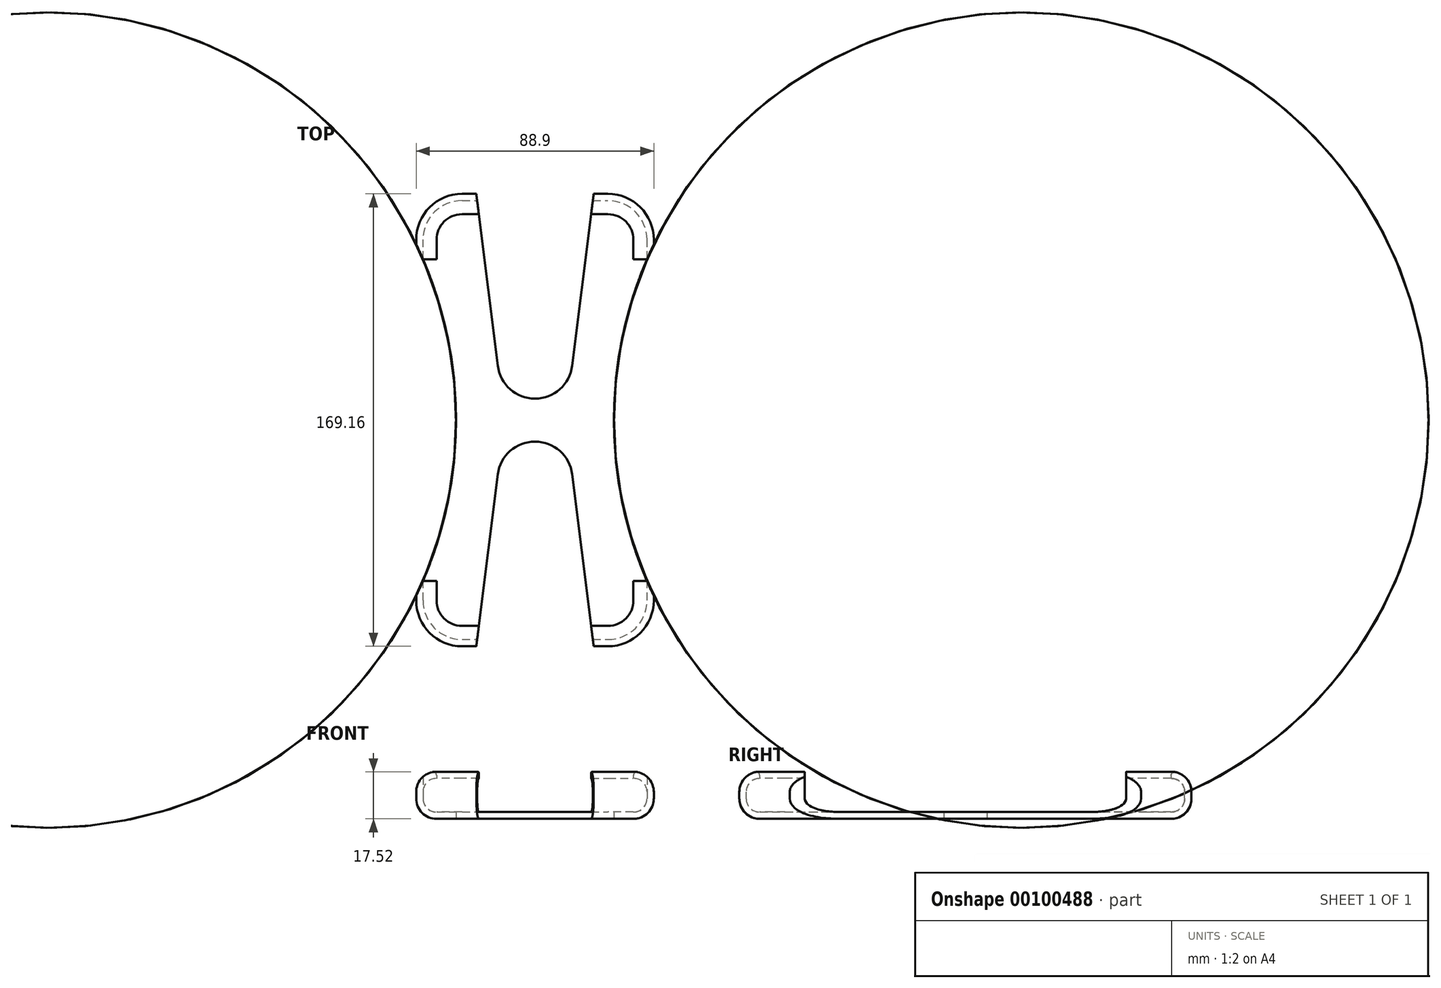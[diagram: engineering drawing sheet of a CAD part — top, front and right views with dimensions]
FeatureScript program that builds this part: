
annotation { "Feature Type Name" : "Feature", "Feature Type Description" : "" }
export const myFeature = defineFeature(function(context is Context, id is Id, definition is map)
    precondition{}
    {
        {
            var Q0;
            Q0=qCreatedBy(makeId("Top.planeOp"),FACE);
            var sketch = newSketch(context, id + "F0", { "sketchPlane" : qUnion([Q0])});
            skLineSegment(sketch, "E0.bottom", {"start": v(-27.3, 84.58) * mm, "end": v(27.3, 84.58) * mm});
            skLineSegment(sketch, "E0.top", {"start": v(-27.3, -84.58) * mm, "end": v(27.3, -84.58) * mm});
            skLineSegment(sketch, "E0.left", {"start": v(-44.45, 67.44) * mm, "end": v(-44.45, -67.44) * mm});
            skLineSegment(sketch, "E0.right", {"start": v(44.45, 67.44) * mm, "end": v(44.45, -67.44) * mm});
            skLineSegment(sketch, "E1", {"start": v(-67.17, 0) * mm, "end": v(67.9, 0) * mm, "construction": true});
            skLineSegment(sketch, "E2", {"start": v(0, 68.28) * mm, "end": v(0, -73.49) * mm, "construction": true});
            skPoint(sketch, "E3.visualSharp", {"position": v(-44.45, 84.58) * mm});
            skArc(sketch, "E3.filletArc", {"start": v(-27.3, 84.58) * mm, "mid": v(-39.43, 79.56) * mm, "end": v(-44.45, 67.44) * mm});
            skPoint(sketch, "E4.visualSharp", {"position": v(44.45, 84.58) * mm});
            skArc(sketch, "E4.filletArc", {"start": v(44.45, 67.44) * mm, "mid": v(39.43, 79.56) * mm, "end": v(27.3, 84.58) * mm});
            skPoint(sketch, "E5.visualSharp", {"position": v(-44.45, -84.58) * mm});
            skArc(sketch, "E5.filletArc", {"start": v(-44.45, -67.44) * mm, "mid": v(-39.43, -79.56) * mm, "end": v(-27.3, -84.58) * mm});
            skPoint(sketch, "E6.visualSharp", {"position": v(44.45, -84.58) * mm});
            skArc(sketch, "E6.filletArc", {"start": v(27.3, -84.58) * mm, "mid": v(39.43, -79.56) * mm, "end": v(44.45, -67.44) * mm});
            skSolve(sketch);
        }
        {
            var Q0;
            Q0=makeQuery(id+"F0.imprint","IMPRINT",FACE,{"disambiguationData":[TD([[makeQuery(id+"F0.imprint","IMPRINT",EDGE,{"derivedFrom":sQuery(id+"F0.wireOp",EDGE,"E0.bottom")}),-1.0]])]});
            extrude(context, id + "F1", {"entities" : qUnion([Q0]), "depth" : 17.65 * mm});
        }
        {
            var Q0;
            Q0=makeQuery(id+"F1.opExtrude","CAP_FACE",FACE,{"disambiguationData":[OSD([sQuery(id+"F0.wireOp",EDGE,"E0.bottom"),sQuery(id+"F0.wireOp",EDGE,"E0.top"),sQuery(id+"F0.wireOp",EDGE,"E0.left"),sQuery(id+"F0.wireOp",EDGE,"E0.right"),sQuery(id+"F0.wireOp",EDGE,"E3.filletArc"),sQuery(id+"F0.wireOp",EDGE,"E4.filletArc"),sQuery(id+"F0.wireOp",EDGE,"E5.filletArc"),sQuery(id+"F0.wireOp",EDGE,"E6.filletArc")])],"isStart":false});
            var Q1;
            Q1=makeQuery(id+"F1.opExtrude","CAP_FACE",FACE,{"disambiguationData":[OSD([sQuery(id+"F0.wireOp",EDGE,"E0.bottom"),sQuery(id+"F0.wireOp",EDGE,"E0.top"),sQuery(id+"F0.wireOp",EDGE,"E0.left"),sQuery(id+"F0.wireOp",EDGE,"E0.right"),sQuery(id+"F0.wireOp",EDGE,"E3.filletArc"),sQuery(id+"F0.wireOp",EDGE,"E4.filletArc"),sQuery(id+"F0.wireOp",EDGE,"E5.filletArc"),sQuery(id+"F0.wireOp",EDGE,"E6.filletArc")])],"isStart":true});
            fillet(context, id + "F2", {"entities" : qUnion([Q0, Q1]), "radius" : 7.62 * mm, "tangentPropagation" : true, "allowEdgeOverflow" : false});
        }
        {
            var Q0;
            Q0=makeQuery(id+"F1.opExtrude","CAP_FACE",FACE,{"disambiguationData":[OSD([sQuery(id+"F0.wireOp",EDGE,"E0.bottom"),sQuery(id+"F0.wireOp",EDGE,"E0.top"),sQuery(id+"F0.wireOp",EDGE,"E0.left"),sQuery(id+"F0.wireOp",EDGE,"E0.right"),sQuery(id+"F0.wireOp",EDGE,"E3.filletArc"),sQuery(id+"F0.wireOp",EDGE,"E4.filletArc"),sQuery(id+"F0.wireOp",EDGE,"E5.filletArc"),sQuery(id+"F0.wireOp",EDGE,"E6.filletArc")])],"isStart":false});
            shell(context, id + "F3", {"entities" : qUnion([Q0]), "thickness" : 2.54 * mm});
        }
        {
            var Q0;
            Q0=qCreatedBy(makeId("Top.planeOp"),FACE);
            var sketch = newSketch(context, id + "F4", { "sketchPlane" : qUnion([Q0])});
            skArc(sketch, "E7", {"start": v(-13.93, 20.34) * mm, "mid": v(0, 8.04) * mm, "end": v(13.93, 20.34) * mm});
            skLineSegment(sketch, "E8", {"start": v(13.93, 20.34) * mm, "end": v(22.47, 88.76) * mm});
            skLineSegment(sketch, "E9", {"start": v(-13.93, 20.34) * mm, "end": v(-22.47, 88.76) * mm});
            skLineSegment(sketch, "E10", {"start": v(-22.47, 88.76) * mm, "end": v(22.47, 88.76) * mm});
            skLineSegment(sketch, "E11", {"start": v(-99.7, 0) * mm, "end": v(84.35, 0) * mm, "construction": true});
            skLineSegment(sketch, "E12.MirrorCS", {"start": v(-22.47, -88.76) * mm, "end": v(22.47, -88.76) * mm});
            skLineSegment(sketch, "E13.MirrorCS", {"start": v(-13.93, -20.34) * mm, "end": v(-22.47, -88.76) * mm});
            skLineSegment(sketch, "E14.MirrorCS", {"start": v(13.93, -20.34) * mm, "end": v(22.47, -88.76) * mm});
            skArc(sketch, "E15.MirrorCS", {"start": v(-13.93, -20.34) * mm, "mid": v(0, -8.04) * mm, "end": v(13.93, -20.34) * mm});
            skSolve(sketch);
        }
        {
            var Q0;
            Q0=makeQuery(id+"F4.imprint","IMPRINT",FACE,{"disambiguationData":[TD([[makeQuery(id+"F4.imprint","IMPRINT",EDGE,{"derivedFrom":sQuery(id+"F4.wireOp",EDGE,"E7")}),1.0]])]});
            var Q1;
            Q1=makeQuery(id+"F4.imprint","IMPRINT",FACE,{"disambiguationData":[TD([[makeQuery(id+"F4.imprint","IMPRINT",EDGE,{"derivedFrom":sQuery(id+"F4.wireOp",EDGE,"E12.MirrorCS")}),1.0]])]});
            extrude(context, id + "F5", {"entities" : qUnion([Q0, Q1]), "operationType" : NewBodyOperationType.REMOVE, "endBound" : BoundingType.THROUGH_ALL, "depth" : 25.4 * mm});
        }
        {
            var Q0;
            Q0=qCreatedBy(makeId("Top.planeOp"),FACE);
            var sketch = newSketch(context, id + "F6", { "sketchPlane" : qUnion([Q0])});
            skArc(sketch, "E16", {"start": v(53.84, 82.55) * mm, "mid": v(29.55, 0) * mm, "end": v(53.84, -82.55) * mm});
            skLineSegment(sketch, "E17", {"start": v(53.84, 82.55) * mm, "end": v(53.84, -82.55) * mm});
            skLineSegment(sketch, "E18", {"start": v(0, 102.51) * mm, "end": v(0, -113.35) * mm, "construction": true});
            skLineSegment(sketch, "E19.MirrorCS", {"start": v(-53.84, 82.55) * mm, "end": v(-53.84, -82.55) * mm});
            skArc(sketch, "E20.MirrorCS", {"start": v(-53.84, 82.55) * mm, "mid": v(-29.55, 0) * mm, "end": v(-53.84, -82.55) * mm});
            skSolve(sketch);
        }
        {
            var Q0;
            Q0=makeQuery(id+"F6.imprint","IMPRINT",FACE,{"disambiguationData":[TD([[makeQuery(id+"F6.imprint","IMPRINT",EDGE,{"derivedFrom":sQuery(id+"F6.wireOp",EDGE,"E16")}),1.0]])]});
            var Q1;
            Q1=makeQuery(id+"F6.imprint","IMPRINT",FACE,{"disambiguationData":[TD([[makeQuery(id+"F6.imprint","IMPRINT",EDGE,{"derivedFrom":sQuery(id+"F6.wireOp",EDGE,"E19.MirrorCS")}),1.0]])]});
            extrude(context, id + "F7", {"entities" : qUnion([Q0, Q1]), "operationType" : NewBodyOperationType.REMOVE, "endBound" : BoundingType.THROUGH_ALL, "depth" : 22.37 * mm});
        }
        {
            var Q0;
            Q0=qCreatedBy(makeId("Right.planeOp"),FACE);
            var sketch = newSketch(context, id + "F8", { "sketchPlane" : qUnion([Q0])});
            skLineSegment(sketch, "E21", {"start": v(0, 37.02) * mm, "end": v(0, -19.18) * mm, "construction": true});
            skLineSegment(sketch, "E22.bottom", {"start": v(-60.13, 7.54) * mm, "end": v(-25.5, 7.54) * mm});
            skLineSegment(sketch, "E22.top", {"start": v(-60.13, 21.67) * mm, "end": v(-25.5, 21.67) * mm});
            skLineSegment(sketch, "E22.left", {"start": v(-60.13, 7.54) * mm, "end": v(-60.13, 21.67) * mm});
            skLineSegment(sketch, "E22.right", {"start": v(-25.5, 7.54) * mm, "end": v(-25.5, 21.67) * mm});
            skLineSegment(sketch, "E23.MirrorCS", {"start": v(60.13, 21.67) * mm, "end": v(25.5, 21.67) * mm});
            skLineSegment(sketch, "E24.MirrorCS", {"start": v(60.13, 7.54) * mm, "end": v(60.13, 21.67) * mm});
            skLineSegment(sketch, "E25.MirrorCS", {"start": v(60.13, 7.54) * mm, "end": v(25.5, 7.54) * mm});
            skLineSegment(sketch, "E26.MirrorCS", {"start": v(25.5, 7.54) * mm, "end": v(25.5, 21.67) * mm});
            skSolve(sketch);
        }
        {
            var Q0;
            Q0=makeQuery(id+"F8.imprint","IMPRINT",FACE,{"disambiguationData":[TD([[makeQuery(id+"F8.imprint","IMPRINT",EDGE,{"derivedFrom":sQuery(id+"F8.wireOp",EDGE,"E22.bottom")}),1.0]])]});
            var Q1;
            Q1=makeQuery(id+"F8.imprint","IMPRINT",FACE,{"disambiguationData":[TD([[makeQuery(id+"F8.imprint","IMPRINT",EDGE,{"derivedFrom":sQuery(id+"F8.wireOp",EDGE,"E23.MirrorCS")}),1.0]])]});
            extrude(context, id + "F9", {"entities" : qUnion([Q0, Q1]), "operationType" : NewBodyOperationType.REMOVE, "endBound" : BoundingType.SYMMETRIC, "oppositeDirection" : true, "depth" : 106.18 * mm});
        }
        {
            var Q0;
            {var subQ0=sQuery(id+"F0.wireOp",EDGE,"E3.filletArc");Q0=makeQuery(id+"F2.opFillet","BLEND_EDGE",EDGE,{"blendedFrom":[makeQuery(id+"F1.opExtrude","CAP_EDGE",EDGE,{"disambiguationData":[OSD([subQ0])],"isStart":false}),makeQuery(id+"F1.opExtrude","CAP_FACE",FACE,{"disambiguationData":[OSD([sQuery(id+"F0.wireOp",EDGE,"E0.bottom"),sQuery(id+"F0.wireOp",EDGE,"E0.top"),sQuery(id+"F0.wireOp",EDGE,"E0.left"),sQuery(id+"F0.wireOp",EDGE,"E0.right"),subQ0,sQuery(id+"F0.wireOp",EDGE,"E4.filletArc"),sQuery(id+"F0.wireOp",EDGE,"E5.filletArc"),sQuery(id+"F0.wireOp",EDGE,"E6.filletArc")])],"isStart":false})],"blendedInto":[makeQuery(id+"F1.opExtrude","CAP_FACE",FACE,{"disambiguationData":[OSD([sQuery(id+"F0.wireOp",EDGE,"E0.bottom"),sQuery(id+"F0.wireOp",EDGE,"E0.top"),sQuery(id+"F0.wireOp",EDGE,"E0.left"),sQuery(id+"F0.wireOp",EDGE,"E0.right"),subQ0,sQuery(id+"F0.wireOp",EDGE,"E4.filletArc"),sQuery(id+"F0.wireOp",EDGE,"E5.filletArc"),sQuery(id+"F0.wireOp",EDGE,"E6.filletArc")])],"isStart":false})]});}
            var Q1;
            {var subQ0=sQuery(id+"F0.wireOp",EDGE,"E5.filletArc");Q1=makeQuery(id+"F2.opFillet","BLEND_EDGE",EDGE,{"blendedFrom":[makeQuery(id+"F1.opExtrude","CAP_EDGE",EDGE,{"disambiguationData":[OSD([subQ0])],"isStart":false}),makeQuery(id+"F1.opExtrude","CAP_FACE",FACE,{"disambiguationData":[OSD([sQuery(id+"F0.wireOp",EDGE,"E0.bottom"),sQuery(id+"F0.wireOp",EDGE,"E0.top"),sQuery(id+"F0.wireOp",EDGE,"E0.left"),sQuery(id+"F0.wireOp",EDGE,"E0.right"),sQuery(id+"F0.wireOp",EDGE,"E3.filletArc"),sQuery(id+"F0.wireOp",EDGE,"E4.filletArc"),subQ0,sQuery(id+"F0.wireOp",EDGE,"E6.filletArc")])],"isStart":false})],"blendedInto":[makeQuery(id+"F1.opExtrude","CAP_FACE",FACE,{"disambiguationData":[OSD([sQuery(id+"F0.wireOp",EDGE,"E0.bottom"),sQuery(id+"F0.wireOp",EDGE,"E0.top"),sQuery(id+"F0.wireOp",EDGE,"E0.left"),sQuery(id+"F0.wireOp",EDGE,"E0.right"),sQuery(id+"F0.wireOp",EDGE,"E3.filletArc"),sQuery(id+"F0.wireOp",EDGE,"E4.filletArc"),subQ0,sQuery(id+"F0.wireOp",EDGE,"E6.filletArc")])],"isStart":false})]});}
            var Q2;
            {var subQ0=sQuery(id+"F0.wireOp",EDGE,"E6.filletArc");Q2=makeQuery(id+"F2.opFillet","BLEND_EDGE",EDGE,{"blendedFrom":[makeQuery(id+"F1.opExtrude","CAP_EDGE",EDGE,{"disambiguationData":[OSD([subQ0])],"isStart":false}),makeQuery(id+"F1.opExtrude","CAP_FACE",FACE,{"disambiguationData":[OSD([sQuery(id+"F0.wireOp",EDGE,"E0.bottom"),sQuery(id+"F0.wireOp",EDGE,"E0.top"),sQuery(id+"F0.wireOp",EDGE,"E0.left"),sQuery(id+"F0.wireOp",EDGE,"E0.right"),sQuery(id+"F0.wireOp",EDGE,"E3.filletArc"),sQuery(id+"F0.wireOp",EDGE,"E4.filletArc"),sQuery(id+"F0.wireOp",EDGE,"E5.filletArc"),subQ0])],"isStart":false})],"blendedInto":[makeQuery(id+"F1.opExtrude","CAP_FACE",FACE,{"disambiguationData":[OSD([sQuery(id+"F0.wireOp",EDGE,"E0.bottom"),sQuery(id+"F0.wireOp",EDGE,"E0.top"),sQuery(id+"F0.wireOp",EDGE,"E0.left"),sQuery(id+"F0.wireOp",EDGE,"E0.right"),sQuery(id+"F0.wireOp",EDGE,"E3.filletArc"),sQuery(id+"F0.wireOp",EDGE,"E4.filletArc"),sQuery(id+"F0.wireOp",EDGE,"E5.filletArc"),subQ0])],"isStart":false})]});}
            var Q3;
            {var subQ0=sQuery(id+"F0.wireOp",EDGE,"E4.filletArc");Q3=makeQuery(id+"F2.opFillet","BLEND_EDGE",EDGE,{"blendedFrom":[makeQuery(id+"F1.opExtrude","CAP_EDGE",EDGE,{"disambiguationData":[OSD([subQ0])],"isStart":false}),makeQuery(id+"F1.opExtrude","CAP_FACE",FACE,{"disambiguationData":[OSD([sQuery(id+"F0.wireOp",EDGE,"E0.bottom"),sQuery(id+"F0.wireOp",EDGE,"E0.top"),sQuery(id+"F0.wireOp",EDGE,"E0.left"),sQuery(id+"F0.wireOp",EDGE,"E0.right"),sQuery(id+"F0.wireOp",EDGE,"E3.filletArc"),subQ0,sQuery(id+"F0.wireOp",EDGE,"E5.filletArc"),sQuery(id+"F0.wireOp",EDGE,"E6.filletArc")])],"isStart":false})],"blendedInto":[makeQuery(id+"F1.opExtrude","CAP_FACE",FACE,{"disambiguationData":[OSD([sQuery(id+"F0.wireOp",EDGE,"E0.bottom"),sQuery(id+"F0.wireOp",EDGE,"E0.top"),sQuery(id+"F0.wireOp",EDGE,"E0.left"),sQuery(id+"F0.wireOp",EDGE,"E0.right"),sQuery(id+"F0.wireOp",EDGE,"E3.filletArc"),subQ0,sQuery(id+"F0.wireOp",EDGE,"E5.filletArc"),sQuery(id+"F0.wireOp",EDGE,"E6.filletArc")])],"isStart":false})]});}
            fillet(context, id + "F10", {"entities" : qUnion([Q0, Q1, Q2, Q3]), "radius" : 1.27 * mm, "tangentPropagation" : true, "allowEdgeOverflow" : false});
        }
    });
